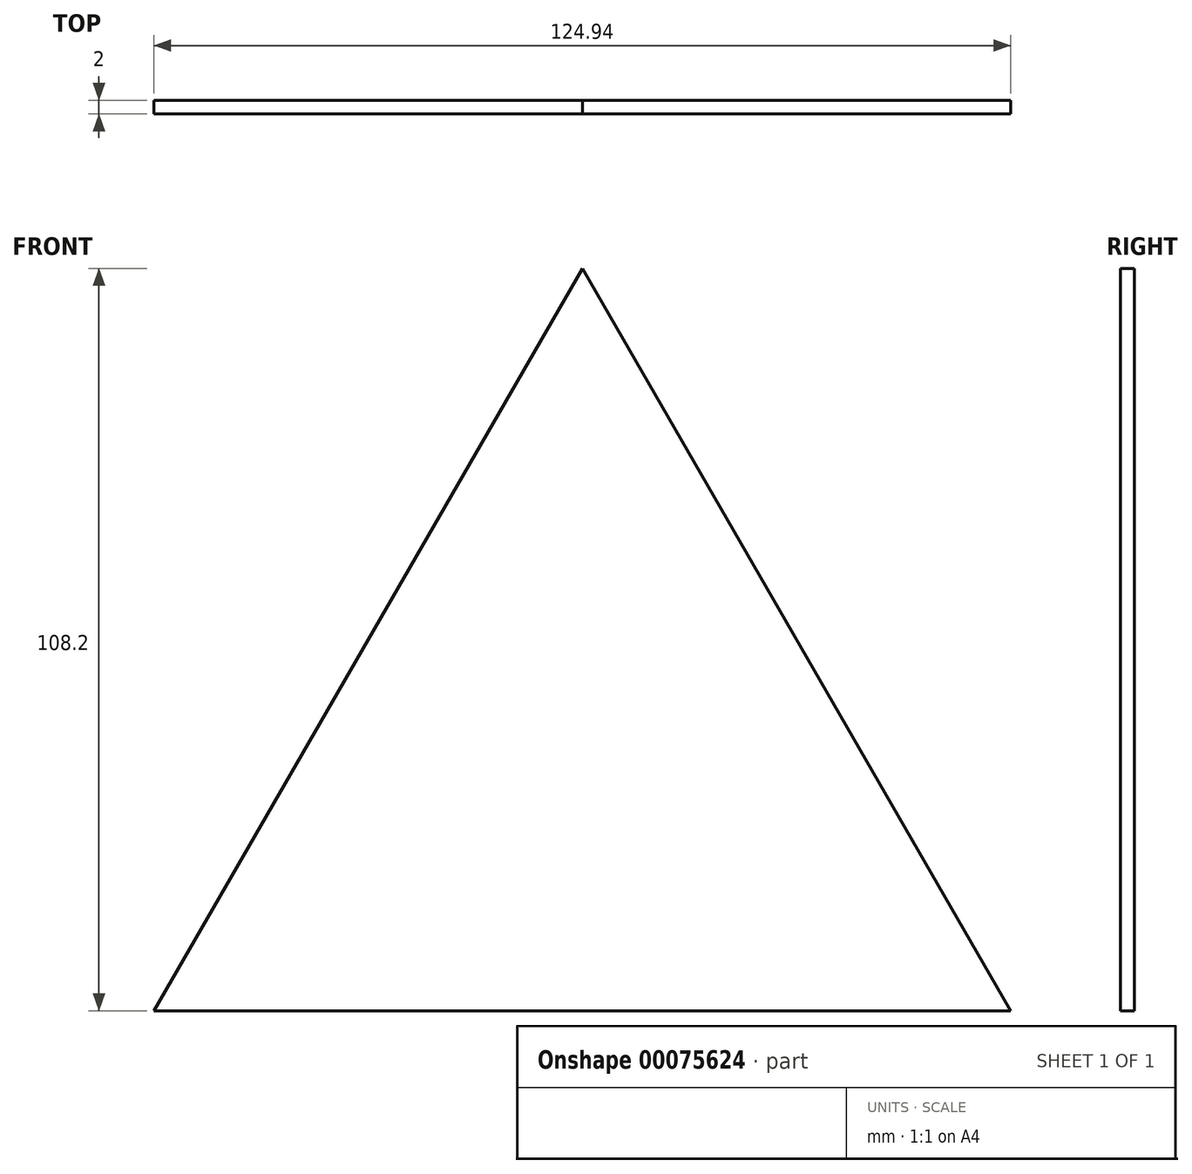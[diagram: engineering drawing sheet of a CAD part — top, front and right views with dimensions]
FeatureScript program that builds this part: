
annotation { "Feature Type Name" : "Feature", "Feature Type Description" : "" }
export const myFeature = defineFeature(function(context is Context, id is Id, definition is map)
    precondition{}
    {
        {
            var Q0;
            Q0=qCreatedBy(makeId("Front.planeOp"),FACE);
            var sketch = newSketch(context, id + "F0", { "sketchPlane" : qUnion([Q0])});
            skLineSegment(sketch, "E0", {"start": v(514.45, 11.44) * mm, "end": v(514.45, 11.44) * mm});
            skLineSegment(sketch, "E1", {"start": v(451.98, -96.76) * mm, "end": v(514.45, -96.76) * mm});
            skLineSegment(sketch, "E2", {"start": v(576.92, -96.76) * mm, "end": v(514.45, 11.44) * mm});
            skLineSegment(sketch, "E3", {"start": v(514.45, 161.44) * mm, "end": v(514.45, 11.44) * mm, "construction": true});
            skLineSegment(sketch, "E4", {"start": v(576.92, -96.76) * mm, "end": v(706.82, -171.76) * mm, "construction": true});
            skPoint(sketch, "E5", {"position": v(514.45, -60.7) * mm});
            skPoint(sketch, "E6", {"position": v(483.22, -42.66) * mm});
            skPoint(sketch, "E7", {"position": v(514.45, -96.76) * mm});
            skPoint(sketch, "E8", {"position": v(545.68, -42.66) * mm});
            skLineSegment(sketch, "E9", {"start": v(483.22, -42.66) * mm, "end": v(451.98, -96.76) * mm});
            skLineSegment(sketch, "E10", {"start": v(514.45, 11.44) * mm, "end": v(483.22, -42.66) * mm});
            skLineSegment(sketch, "E11", {"start": v(514.45, -96.76) * mm, "end": v(576.92, -96.76) * mm});
            skLineSegment(sketch, "E12", {"start": v(483.22, -42.66) * mm, "end": v(576.92, -96.76) * mm, "construction": true});
            skLineSegment(sketch, "E13", {"start": v(514.45, -96.76) * mm, "end": v(514.45, -246.76) * mm, "construction": true});
            skLineSegment(sketch, "E14", {"start": v(514.45, 11.44) * mm, "end": v(514.45, -96.76) * mm, "construction": true});
            skLineSegment(sketch, "E15", {"start": v(353.31, 32.34) * mm, "end": v(483.22, -42.66) * mm, "construction": true});
            skLineSegment(sketch, "E16.MirrorCS", {"start": v(451.98, -96.76) * mm, "end": v(322.08, -171.76) * mm, "construction": true});
            skLineSegment(sketch, "E17.MirrorCS", {"start": v(675.59, 32.34) * mm, "end": v(545.68, -42.66) * mm, "construction": true});
            skLineSegment(sketch, "E18.MirrorCS", {"start": v(545.68, -42.66) * mm, "end": v(451.98, -96.76) * mm, "construction": true});
            skLineSegment(sketch, "E19", {"start": v(514.45, -60.7) * mm, "end": v(535.27, -96.76) * mm, "construction": true});
            skLineSegment(sketch, "E20", {"start": v(706.1, -60.7) * mm, "end": v(556.1, -60.7) * mm, "construction": true});
            skLineSegment(sketch, "E21", {"start": v(514.45, -60.7) * mm, "end": v(535.27, -24.63) * mm, "construction": true});
            skLineSegment(sketch, "E22", {"start": v(418.63, 105.27) * mm, "end": v(493.63, -24.63) * mm, "construction": true});
            skLineSegment(sketch, "E23", {"start": v(514.45, -60.7) * mm, "end": v(472.8, -60.7) * mm, "construction": true});
            skLineSegment(sketch, "E24", {"start": v(418.63, -226.67) * mm, "end": v(493.63, -96.76) * mm, "construction": true});
            skLineSegment(sketch, "E25", {"start": v(535.27, -24.63) * mm, "end": v(610.27, 105.27) * mm, "construction": true});
            skLineSegment(sketch, "E26", {"start": v(493.63, -24.63) * mm, "end": v(514.45, -60.7) * mm, "construction": true});
            skLineSegment(sketch, "E27", {"start": v(472.8, -60.7) * mm, "end": v(322.8, -60.7) * mm, "construction": true});
            skLineSegment(sketch, "E28", {"start": v(493.63, -96.76) * mm, "end": v(514.45, -60.7) * mm, "construction": true});
            skLineSegment(sketch, "E29", {"start": v(535.27, -96.76) * mm, "end": v(610.27, -226.67) * mm, "construction": true});
            skLineSegment(sketch, "E30", {"start": v(556.1, -60.7) * mm, "end": v(514.45, -60.7) * mm, "construction": true});
            skSolve(sketch);
        }
        {
            var Q0;
            Q0=makeQuery(id+"F0.imprint","IMPRINT",FACE,{"disambiguationData":[TD([[makeQuery(id+"F0.imprint","IMPRINT",EDGE,{"derivedFrom":sQuery(id+"F0.wireOp",EDGE,"E1")}),1.0]])]});
            var Q1;
            Q1=sQuery(id+"F0.wireOp",EDGE,"E10");
            var Q2;
            Q2=sQuery(id+"F0.wireOp",EDGE,"E2");
            var Q3;
            Q3=sQuery(id+"F0.wireOp",EDGE,"E11");
            var Q4;
            Q4=sQuery(id+"F0.wireOp",EDGE,"E1");
            var Q5;
            Q5=sQuery(id+"F0.wireOp",EDGE,"E9");
            extrude(context, id + "F1", {"entities" : qUnion([Q0]), "surfaceEntities" : qUnion([Q1, Q2, Q3, Q4, Q5]), "depth" : 2 * mm});
        }
    });
